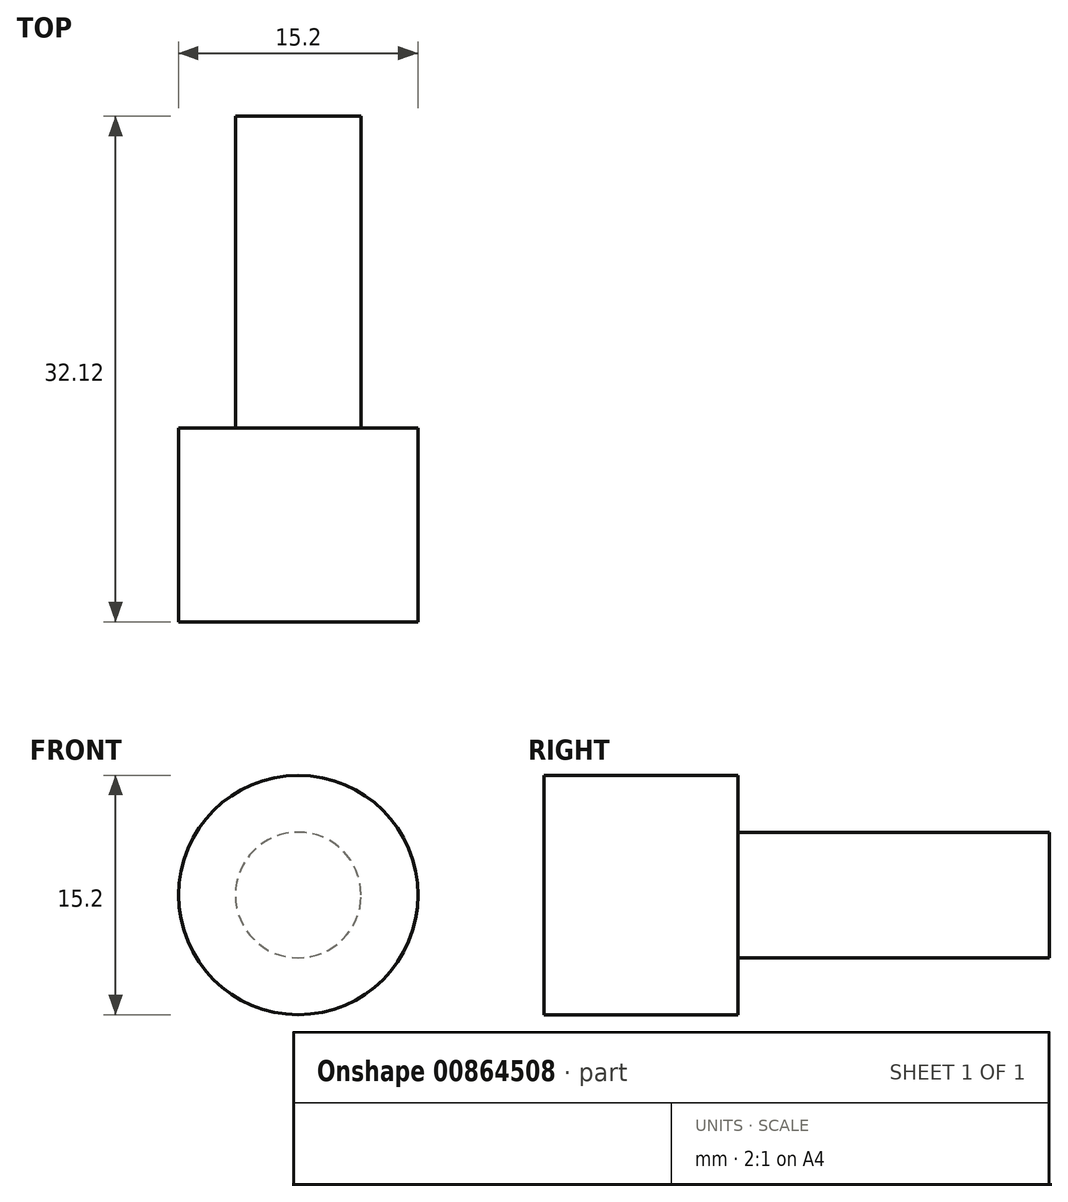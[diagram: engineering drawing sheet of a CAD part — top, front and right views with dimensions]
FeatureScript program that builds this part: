
annotation { "Feature Type Name" : "Feature", "Feature Type Description" : "" }
export const myFeature = defineFeature(function(context is Context, id is Id, definition is map)
    precondition{}
    {
        {
            var Q0;
            Q0=qCreatedBy(makeId("Top.planeOp"),FACE);
            var sketch = newSketch(context, id + "F0", { "sketchPlane" : qUnion([Q0])});
            skLineSegment(sketch, "E0", {"start": v(0, 0) * mm, "end": v(0, 32.12) * mm});
            skLineSegment(sketch, "E1", {"start": v(0, 32.12) * mm, "end": v(3.99, 32.12) * mm});
            skLineSegment(sketch, "E2", {"start": v(4, 32.12) * mm, "end": v(4, 12.32) * mm});
            skLineSegment(sketch, "E3", {"start": v(4, 12.32) * mm, "end": v(7.6, 12.32) * mm});
            skLineSegment(sketch, "E4", {"start": v(7.6, 12.32) * mm, "end": v(7.6, 0) * mm});
            skLineSegment(sketch, "E5", {"start": v(7.6, 0) * mm, "end": v(0, 0) * mm});
            skSolve(sketch);
        }
        {
            var Q0;
            Q0=makeQuery(id+"F0.imprint","IMPRINT",FACE,{"disambiguationData":[TD([[makeQuery(id+"F0.imprint","IMPRINT",EDGE,{"derivedFrom":sQuery(id+"F0.wireOp",EDGE,"E0")}),-1.0]])]});
            var Q1;
            Q1=sQuery(id+"F0.wireOp",EDGE,"E0");
            revolve(context, id + "F1", {"surfaceOperationType" : NewSurfaceOperationType.NEW, "entities" : qUnion([Q0]), "axis" : qUnion([Q1]), "revolveType" : RevolveType.FULL});
        }
    });
